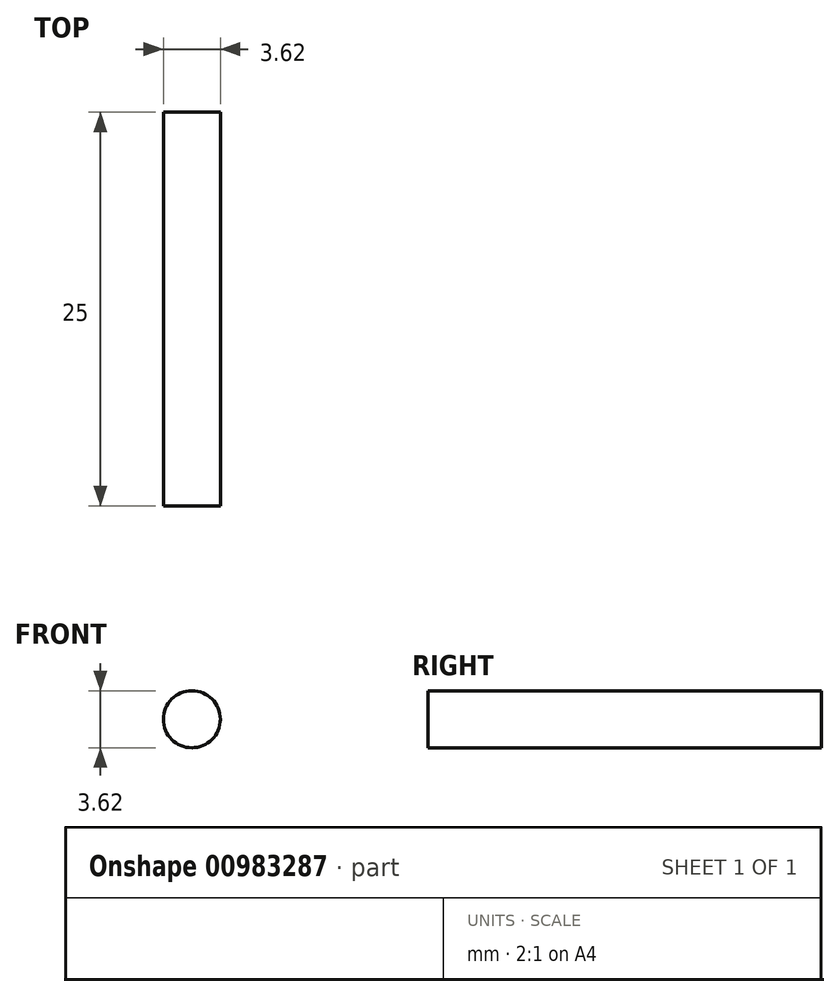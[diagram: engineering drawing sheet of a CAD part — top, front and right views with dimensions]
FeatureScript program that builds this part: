
annotation { "Feature Type Name" : "Feature", "Feature Type Description" : "" }
export const myFeature = defineFeature(function(context is Context, id is Id, definition is map)
    precondition{}
    {
        {
            var Q0;
            Q0=qCreatedBy(makeId("Front.planeOp"),FACE);
            var sketch = newSketch(context, id + "F0", { "sketchPlane" : qUnion([Q0])});
            skCircle(sketch, "E0", {"center": v(0, 0) * mm, "radius": 1.8 * mm});
            skSolve(sketch);
        }
        {
            var Q0;
            Q0 = qSketchRegion(id + "F0", true);
            extrude(context, id + "F1", {"entities" : qUnion([Q0]), "depth" : 25 * mm, "offsetDistance" : 25 * mm});
        }
    });
